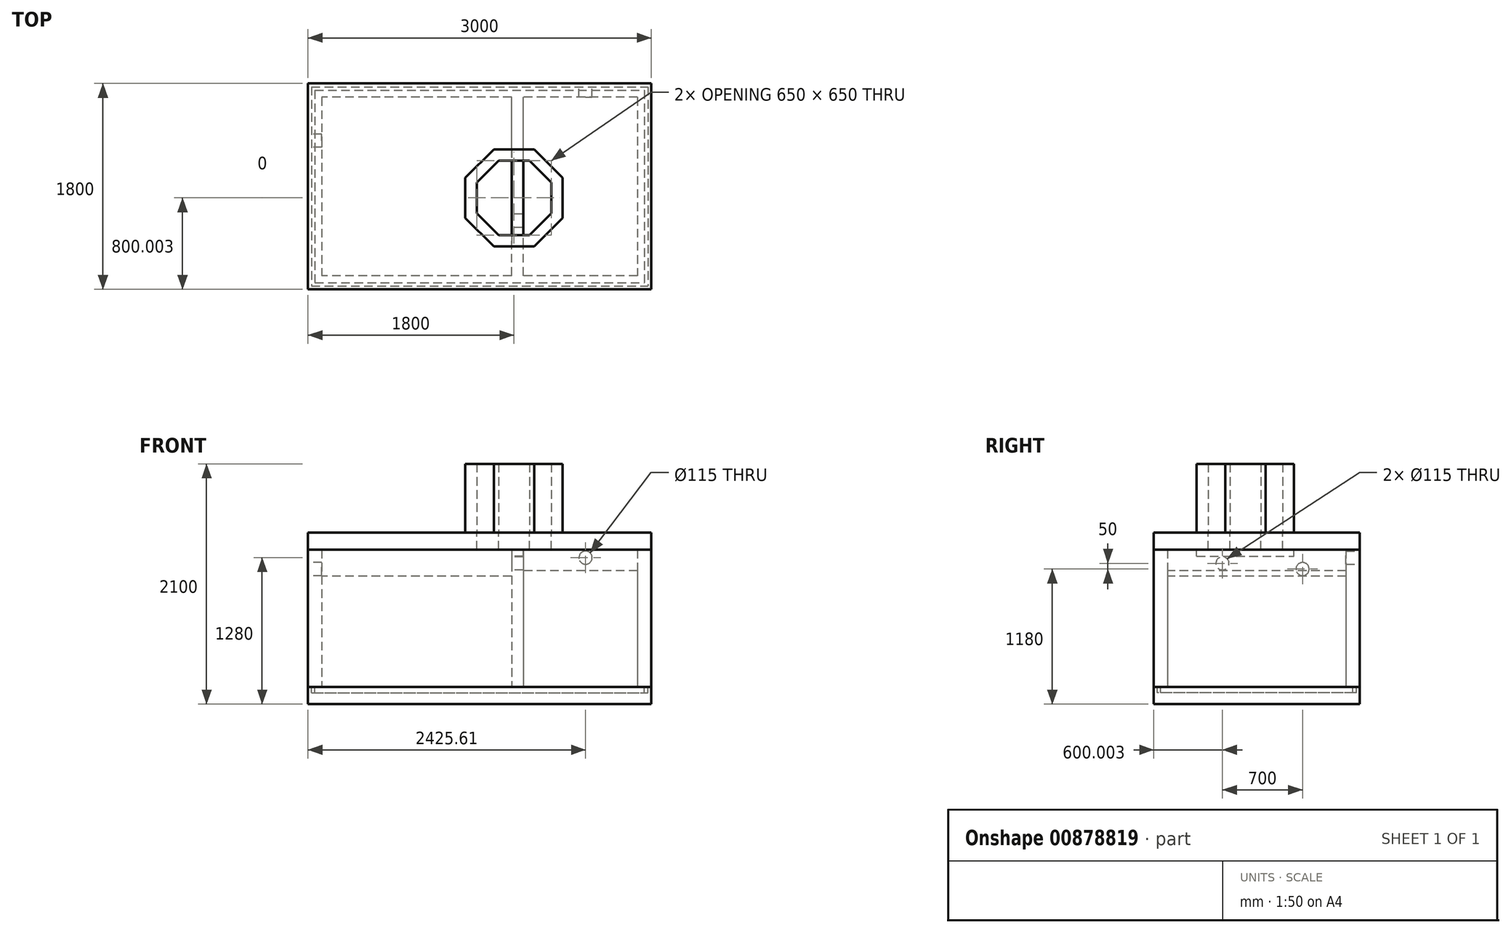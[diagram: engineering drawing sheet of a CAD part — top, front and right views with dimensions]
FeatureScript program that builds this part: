
annotation { "Feature Type Name" : "Feature", "Feature Type Description" : "" }
export const myFeature = defineFeature(function(context is Context, id is Id, definition is map)
    precondition{}
    {
        {
            var Q0;
            Q0=qCreatedBy(makeId("Top.planeOp"),FACE);
            var sketch = newSketch(context, id + "F0", { "sketchPlane" : qUnion([Q0])});
            skLineSegment(sketch, "E0.bottom", {"start": v(-1441.41, 733.1) * mm, "end": v(1558.59, 733.1) * mm});
            skLineSegment(sketch, "E0.top", {"start": v(-1441.41, -1066.9) * mm, "end": v(1558.59, -1066.9) * mm});
            skLineSegment(sketch, "E0.left", {"start": v(-1441.41, 733.1) * mm, "end": v(-1441.41, -1066.9) * mm});
            skLineSegment(sketch, "E0.right", {"start": v(1558.59, 733.1) * mm, "end": v(1558.59, -1066.9) * mm});
            skSolve(sketch);
        }
        {
            var Q0;
            Q0=makeQuery(id+"F0.imprint","IMPRINT",FACE,{"disambiguationData":[TD([[makeQuery(id+"F0.imprint","IMPRINT",EDGE,{"derivedFrom":sQuery(id+"F0.wireOp",EDGE,"E0.bottom")}),-1.0]])]});
            extrude(context, id + "F1", {"entities" : qUnion([Q0]), "depth" : 150 * mm, "offsetDistance" : 25 * mm});
        }
        {
            var Q0;
            Q0=makeQuery(id+"F1.opExtrude","CAP_FACE",FACE,{"disambiguationData":[OSD([sQuery(id+"F0.wireOp",EDGE,"E0.bottom"),sQuery(id+"F0.wireOp",EDGE,"E0.top"),sQuery(id+"F0.wireOp",EDGE,"E0.left"),sQuery(id+"F0.wireOp",EDGE,"E0.right")])],"isStart":false});
            var sketch = newSketch(context, id + "F2", { "sketchPlane" : qUnion([Q0])});
            skLineSegment(sketch, "E1.bottom", {"start": v(-1411.41, 703.1) * mm, "end": v(1528.59, 703.1) * mm});
            skLineSegment(sketch, "E1.top", {"start": v(-1411.41, -1036.9) * mm, "end": v(1528.59, -1036.9) * mm});
            skLineSegment(sketch, "E1.left", {"start": v(-1411.41, 703.1) * mm, "end": v(-1411.41, -1036.9) * mm});
            skLineSegment(sketch, "E1.right", {"start": v(1528.59, 703.1) * mm, "end": v(1528.59, -1036.9) * mm});
            skLineSegment(sketch, "E2.0", {"start": v(-1381.41, 673.1) * mm, "end": v(-1381.41, -1006.9) * mm});
            skLineSegment(sketch, "E2.1", {"start": v(-1381.41, 673.1) * mm, "end": v(1498.59, 673.1) * mm});
            skLineSegment(sketch, "E2.2", {"start": v(1498.59, 673.1) * mm, "end": v(1498.59, -1006.9) * mm});
            skLineSegment(sketch, "E2.3", {"start": v(-1381.41, -1006.9) * mm, "end": v(1498.59, -1006.9) * mm});
            skSolve(sketch);
        }
        {
            var Q0;
            Q0=makeQuery(id+"F2.imprint","IMPRINT",FACE,{"disambiguationData":[TD([[makeQuery(id+"F2.imprint","IMPRINT",EDGE,{"derivedFrom":sQuery(id+"F2.wireOp",EDGE,"E1.bottom")}),-1.0]])]});
            extrude(context, id + "F3", {"entities" : qUnion([Q0]), "operationType" : NewBodyOperationType.REMOVE, "oppositeDirection" : true, "depth" : 50 * mm, "offsetDistance" : 25 * mm});
        }
        {
            var Q0;
            {var subQ0=sQuery(id+"F0.wireOp",EDGE,"E0.left");var subQ1=sQuery(id+"F0.wireOp",EDGE,"E0.top");var subQ2=sQuery(id+"F0.wireOp",EDGE,"E0.right");var subQ3=sQuery(id+"F0.wireOp",EDGE,"E0.bottom");Q0=makeQuery(id+"F3.boolean.opBoolean","SPLIT",FACE,{"disambiguationData":[TD([makeQuery(id+"F1.opExtrude","SWEPT_FACE",FACE,{"disambiguationData":[OSD([subQ3])]})])],"derivedFrom":makeQuery(id+"F1.opExtrude","CAP_FACE",FACE,{"disambiguationData":[OSD([subQ3,subQ1,subQ0,subQ2])],"isStart":false})});}
            var sketch = newSketch(context, id + "F4", { "sketchPlane" : qUnion([Q0])});
            skLineSegment(sketch, "E3.bottom", {"start": v(1558.59, 733.1) * mm, "end": v(-1441.41, 733.1) * mm});
            skLineSegment(sketch, "E3.top", {"start": v(1558.59, -1066.9) * mm, "end": v(-1441.41, -1066.9) * mm});
            skLineSegment(sketch, "E3.left", {"start": v(1558.59, 733.1) * mm, "end": v(1558.59, -1066.9) * mm});
            skLineSegment(sketch, "E3.right", {"start": v(-1441.41, 733.1) * mm, "end": v(-1441.41, -1066.9) * mm});
            skLineSegment(sketch, "E4.0", {"start": v(1438.59, 613.1) * mm, "end": v(1438.59, -946.9) * mm});
            skLineSegment(sketch, "E4.1", {"start": v(1438.59, 613.1) * mm, "end": v(438.59, 613.1) * mm});
            skLineSegment(sketch, "E4.2", {"start": v(-1321.41, 613.1) * mm, "end": v(-1321.41, -946.9) * mm});
            skLineSegment(sketch, "E4.3", {"start": v(1438.59, -946.9) * mm, "end": v(438.59, -946.9) * mm});
            skLineSegment(sketch, "E5", {"start": v(438.59, -946.9) * mm, "end": v(438.59, 613.1) * mm});
            skLineSegment(sketch, "E6.0", {"start": v(338.59, -1166.9) * mm, "end": v(338.59, 628.91) * mm});
            skLineSegment(sketch, "E7", {"start": v(338.59, -946.9) * mm, "end": v(-1321.41, -946.9) * mm});
            skLineSegment(sketch, "E8", {"start": v(338.59, 628.91) * mm, "end": v(338.59, 633.1) * mm});
            skLineSegment(sketch, "E9", {"start": v(338.59, 628.91) * mm, "end": v(338.59, 628.91) * mm});
            skLineSegment(sketch, "E10", {"start": v(338.59, 613.1) * mm, "end": v(-1321.41, 613.1) * mm});
            skSolve(sketch);
        }
        {
            var Q0;
            Q0 = qSketchRegion(id + "F4", true);
            extrude(context, id + "F5", {"entities" : qUnion([Q0]), "depth" : 1200 * mm, "offsetDistance" : 25 * mm});
        }
        {
            var Q0;
            Q0=makeQuery(id+"F5.opExtrude","CAP_FACE",FACE,{"disambiguationData":[OSD([sQuery(id+"F4.wireOp",EDGE,"E3.bottom"),sQuery(id+"F4.wireOp",EDGE,"E3.top"),sQuery(id+"F4.wireOp",EDGE,"E3.left"),sQuery(id+"F4.wireOp",EDGE,"E3.right"),sQuery(id+"F4.wireOp",EDGE,"E4.0"),sQuery(id+"F4.wireOp",EDGE,"E4.1"),sQuery(id+"F4.wireOp",EDGE,"E4.2"),sQuery(id+"F4.wireOp",EDGE,"E4.3"),sQuery(id+"F4.wireOp",EDGE,"E5"),sQuery(id+"F4.wireOp",EDGE,"E6.0"),sQuery(id+"F4.wireOp",EDGE,"E7"),sQuery(id+"F4.wireOp",EDGE,"E8"),sQuery(id+"F4.wireOp",EDGE,"E10")])],"isStart":false});
            var sketch = newSketch(context, id + "F6", { "sketchPlane" : qUnion([Q0])});
            skLineSegment(sketch, "E11.bottom", {"start": v(-1441.41, 733.1) * mm, "end": v(1558.59, 733.1) * mm});
            skLineSegment(sketch, "E11.top", {"start": v(-1441.41, -1066.9) * mm, "end": v(1558.59, -1066.9) * mm});
            skLineSegment(sketch, "E11.left", {"start": v(-1441.41, 733.1) * mm, "end": v(-1441.41, -1066.9) * mm});
            skLineSegment(sketch, "E11.right", {"start": v(1558.59, 733.1) * mm, "end": v(1558.59, -1066.9) * mm});
            skSolve(sketch);
        }
        {
            var Q0;
            Q0 = qSketchRegion(id + "F6", true);
            extrude(context, id + "F7", {"entities" : qUnion([Q0]), "depth" : 150 * mm, "offsetDistance" : 25 * mm});
        }
        {
            var Q0;
            Q0=makeQuery(id+"F5.opExtrude","SWEPT_FACE",FACE,{"disambiguationData":[OSD([sQuery(id+"F4.wireOp",EDGE,"E3.bottom")])]});
            var sketch = newSketch(context, id + "F8", { "sketchPlane" : qUnion([Q0])});
            skPoint(sketch, "E12", {"position": v(-984.2, 1280) * mm});
            skCircle(sketch, "E13", {"center": v(-984.2, 1280) * mm, "radius": 57.5 * mm});
            skSolve(sketch);
        }
        {
            var Q0;
            Q0=makeQuery(id+"F8.imprint","IMPRINT",FACE,{"disambiguationData":[TD([[makeQuery(id+"F8.imprint","IMPRINT",EDGE,{"derivedFrom":sQuery(id+"F8.wireOp",EDGE,"E13")}),1.0]])]});
            extrude(context, id + "F9", {"entities" : qUnion([Q0]), "operationType" : NewBodyOperationType.REMOVE, "oppositeDirection" : true, "depth" : 390 * mm, "offsetDistance" : 25 * mm});
        }
        {
            var Q0;
            Q0=makeQuery(id+"F5.opExtrude","SWEPT_FACE",FACE,{"disambiguationData":[OSD([sQuery(id+"F4.wireOp",EDGE,"E6.0"),sQuery(id+"F4.wireOp",EDGE,"E8")])]});
            var sketch = newSketch(context, id + "F10", { "sketchPlane" : qUnion([Q0])});
            skPoint(sketch, "E14", {"position": v(466.9, 1230) * mm});
            skCircle(sketch, "E15", {"center": v(466.9, 1230) * mm, "radius": 57.5 * mm});
            skSolve(sketch);
        }
        {
            var Q0;
            Q0=makeQuery(id+"F10.imprint","IMPRINT",FACE,{"disambiguationData":[TD([[makeQuery(id+"F10.imprint","IMPRINT",EDGE,{"derivedFrom":sQuery(id+"F10.wireOp",EDGE,"E15")}),1.0]])]});
            extrude(context, id + "F11", {"entities" : qUnion([Q0]), "operationType" : NewBodyOperationType.REMOVE, "oppositeDirection" : true, "depth" : 430 * mm, "offsetDistance" : 25 * mm});
        }
        {
            var Q0;
            Q0=makeQuery(id+"F5.opExtrude","SWEPT_FACE",FACE,{"disambiguationData":[OSD([sQuery(id+"F4.wireOp",EDGE,"E3.right")])]});
            var sketch = newSketch(context, id + "F12", { "sketchPlane" : qUnion([Q0])});
            skPoint(sketch, "E16", {"position": v(-233.1, 1180) * mm});
            skCircle(sketch, "E17", {"center": v(-233.1, 1180) * mm, "radius": 57.5 * mm});
            skSolve(sketch);
        }
        {
            var Q0;
            Q0=makeQuery(id+"F12.imprint","IMPRINT",FACE,{"disambiguationData":[TD([[makeQuery(id+"F12.imprint","IMPRINT",EDGE,{"derivedFrom":sQuery(id+"F12.wireOp",EDGE,"E17")}),1.0]])]});
            extrude(context, id + "F13", {"entities" : qUnion([Q0]), "operationType" : NewBodyOperationType.REMOVE, "oppositeDirection" : true, "depth" : 660 * mm, "offsetDistance" : 25 * mm});
        }
        {
            var Q0;
            Q0=makeQuery(id+"F7.opExtrude","CAP_FACE",FACE,{"disambiguationData":[OSD([sQuery(id+"F6.wireOp",EDGE,"E11.bottom"),sQuery(id+"F6.wireOp",EDGE,"E11.top"),sQuery(id+"F6.wireOp",EDGE,"E11.left"),sQuery(id+"F6.wireOp",EDGE,"E11.right")])],"isStart":false});
            var sketch = newSketch(context, id + "F14", { "sketchPlane" : qUnion([Q0])});
            skCircle(sketch, "E18.cCircle", {"center": v(358.59, -266.9) * mm, "radius": 425 * mm, "construction": true});
            skLineSegment(sketch, "E18.0", {"start": v(-66.41, -90.87) * mm, "end": v(182.55, 158.1) * mm});
            skLineSegment(sketch, "E18.1", {"start": v(182.55, 158.1) * mm, "end": v(534.63, 158.1) * mm});
            skLineSegment(sketch, "E18.2", {"start": v(534.63, 158.1) * mm, "end": v(783.59, -90.87) * mm});
            skLineSegment(sketch, "E18.3", {"start": v(783.59, -90.87) * mm, "end": v(783.59, -442.95) * mm});
            skLineSegment(sketch, "E18.4", {"start": v(783.59, -442.95) * mm, "end": v(534.63, -691.9) * mm});
            skLineSegment(sketch, "E18.5", {"start": v(534.63, -691.9) * mm, "end": v(182.55, -691.9) * mm});
            skLineSegment(sketch, "E18.6", {"start": v(182.55, -691.9) * mm, "end": v(-66.41, -442.95) * mm});
            skLineSegment(sketch, "E18.7", {"start": v(-66.41, -442.95) * mm, "end": v(-66.41, -90.87) * mm});
            skPoint(sketch, "E18.0.midPoint", {"position": v(58.07, 33.61) * mm});
            skLineSegment(sketch, "E19.0", {"start": v(33.59, -401.53) * mm, "end": v(33.59, -132.29) * mm});
            skLineSegment(sketch, "E19.1", {"start": v(223.97, -591.9) * mm, "end": v(33.59, -401.53) * mm});
            skLineSegment(sketch, "E19.2", {"start": v(33.59, -132.29) * mm, "end": v(223.97, 58.1) * mm});
            skLineSegment(sketch, "E19.3", {"start": v(493.2, -591.9) * mm, "end": v(223.97, -591.9) * mm});
            skLineSegment(sketch, "E19.4", {"start": v(223.97, 58.1) * mm, "end": v(493.2, 58.1) * mm});
            skLineSegment(sketch, "E19.5", {"start": v(493.2, 58.1) * mm, "end": v(683.59, -132.29) * mm});
            skLineSegment(sketch, "E19.6", {"start": v(683.59, -132.29) * mm, "end": v(683.59, -401.53) * mm});
            skLineSegment(sketch, "E19.7", {"start": v(683.59, -401.53) * mm, "end": v(493.2, -591.9) * mm});
            skLineSegment(sketch, "E20.0.0", {"start": v(1558.59, 733.1) * mm, "end": v(-1441.41, 733.1) * mm});
            skLineSegment(sketch, "E20.0.1", {"start": v(-1441.41, 733.1) * mm, "end": v(-1441.41, -1066.9) * mm});
            skLineSegment(sketch, "E20.0.2", {"start": v(-1441.41, -1066.9) * mm, "end": v(1558.59, -1066.9) * mm});
            skLineSegment(sketch, "E20.0.3", {"start": v(1558.59, -1066.9) * mm, "end": v(1558.59, 733.1) * mm});
            skSolve(sketch);
        }
        {
            var Q0;
            Q0=makeQuery(id+"F14.imprint","IMPRINT",FACE,{"disambiguationData":[TD([[makeQuery(id+"F14.imprint","IMPRINT",EDGE,{"derivedFrom":sQuery(id+"F14.wireOp",EDGE,"E19.0")}),-1.0]])]});
            extrude(context, id + "F15", {"entities" : qUnion([Q0]), "operationType" : NewBodyOperationType.REMOVE, "endBound" : BoundingType.UP_TO_NEXT, "oppositeDirection" : true, "depth" : 25 * mm, "offsetDistance" : 25 * mm});
        }
        {
            var Q0;
            Q0=makeQuery(id+"F14.imprint","IMPRINT",FACE,{"disambiguationData":[TD([[makeQuery(id+"F14.imprint","IMPRINT",EDGE,{"derivedFrom":sQuery(id+"F14.wireOp",EDGE,"E18.0")}),-1.0]])]});
            extrude(context, id + "F16", {"entities" : qUnion([Q0]), "depth" : 600 * mm, "offsetDistance" : 25 * mm});
        }
        {
            var Q0;
            Q0=makeQuery(id+"F5.opExtrude","SWEPT_FACE",FACE,{"disambiguationData":[OSD([sQuery(id+"F4.wireOp",EDGE,"E6.0")])]});
            var sketch = newSketch(context, id + "F17", { "sketchPlane" : qUnion([Q0])});
            skLineSegment(sketch, "E21.0", {"start": v(-158.1, 2100) * mm, "end": v(-158.1, 1500) * mm});
            skLineSegment(sketch, "E22.0", {"start": v(691.9, 2100) * mm, "end": v(691.9, 1500) * mm});
            skLineSegment(sketch, "E23.bottom", {"start": v(-158.1, 1500) * mm, "end": v(691.9, 1500) * mm});
            skLineSegment(sketch, "E23.top", {"start": v(-158.1, 1500) * mm, "end": v(691.9, 1500) * mm});
            skLineSegment(sketch, "E23.left", {"start": v(-158.1, 1500) * mm, "end": v(-158.1, 1500) * mm});
            skLineSegment(sketch, "E23.right", {"start": v(691.9, 1500) * mm, "end": v(691.9, 1500) * mm});
            skLineSegment(sketch, "E24", {"start": v(-158.1, 1500) * mm, "end": v(-158.1, 1237.18) * mm, "construction": true});
            skLineSegment(sketch, "E25", {"start": v(691.9, 1500) * mm, "end": v(691.9, 1209.25) * mm, "construction": true});
            skLineSegment(sketch, "E26.bottom", {"start": v(-158.1, 1350) * mm, "end": v(691.9, 1350) * mm});
            skLineSegment(sketch, "E26.top", {"start": v(-158.1, 1293.04) * mm, "end": v(691.9, 1293.04) * mm});
            skLineSegment(sketch, "E26.left", {"start": v(-158.1, 1350) * mm, "end": v(-158.1, 1293.04) * mm});
            skLineSegment(sketch, "E26.right", {"start": v(691.9, 1350) * mm, "end": v(691.9, 1293.04) * mm});
            skSolve(sketch);
        }
        {
            var Q0;
            Q0=makeQuery(id+"F17.imprint","IMPRINT",FACE,{"disambiguationData":[TD([[makeQuery(id+"F17.imprint","IMPRINT",EDGE,{"derivedFrom":sQuery(id+"F17.wireOp",EDGE,"E26.bottom")}),1.0]])]});
            extrude(context, id + "F18", {"entities" : qUnion([Q0]), "operationType" : NewBodyOperationType.REMOVE, "endBound" : BoundingType.UP_TO_NEXT, "oppositeDirection" : true, "depth" : 25 * mm, "offsetDistance" : 25 * mm});
        }
        {
            var Q0;
            Q0=makeQuery(id+"F3.boolean.opBoolean","SPLIT",FACE,{"disambiguationData":[TD([makeQuery(id+"F3.opExtrude","SWEPT_FACE",FACE,{"disambiguationData":[OSD([sQuery(id+"F2.wireOp",EDGE,"E2.0")])]})])],"derivedFrom":makeQuery(id+"F1.opExtrude","CAP_FACE",FACE,{"disambiguationData":[OSD([sQuery(id+"F0.wireOp",EDGE,"E0.bottom"),sQuery(id+"F0.wireOp",EDGE,"E0.top"),sQuery(id+"F0.wireOp",EDGE,"E0.left"),sQuery(id+"F0.wireOp",EDGE,"E0.right")])],"isStart":false})});
            var sketch = newSketch(context, id + "F19", { "sketchPlane" : qUnion([Q0])});
            skLineSegment(sketch, "E27.0", {"start": v(-1321.41, 613.1) * mm, "end": v(-1321.41, -946.9) * mm});
            skLineSegment(sketch, "E28.0", {"start": v(338.59, 613.1) * mm, "end": v(-1321.41, 613.1) * mm});
            skLineSegment(sketch, "E29.0", {"start": v(338.59, -946.9) * mm, "end": v(-1321.41, -946.9) * mm});
            skLineSegment(sketch, "E30.0", {"start": v(338.59, -946.9) * mm, "end": v(338.59, 613.1) * mm});
            skSolve(sketch);
        }
        {
            var Q0;
            Q0=makeQuery(id+"F19.imprint","IMPRINT",FACE,{"disambiguationData":[TD([[makeQuery(id+"F19.imprint","IMPRINT",EDGE,{"derivedFrom":sQuery(id+"F19.wireOp",EDGE,"E27.0")}),-1.0]])]});
            var sketch = newSketch(context, id + "F20", { "sketchPlane" : qUnion([Q0])});
            skLineSegment(sketch, "E31.0", {"start": v(1438.59, 613.1) * mm, "end": v(438.59, 613.1) * mm});
            skLineSegment(sketch, "E32.0", {"start": v(1438.59, 613.1) * mm, "end": v(1438.59, -946.9) * mm});
            skLineSegment(sketch, "E33.0", {"start": v(1438.59, -946.9) * mm, "end": v(438.59, -946.9) * mm});
            skLineSegment(sketch, "E34.0", {"start": v(438.59, -946.9) * mm, "end": v(438.59, 613.1) * mm});
            skSolve(sketch);
        }
        {
            var Q0;
            Q0=makeQuery(id+"F20.imprint","IMPRINT",FACE,{"disambiguationData":[TD([[makeQuery(id+"F20.imprint","IMPRINT",EDGE,{"derivedFrom":sQuery(id+"F20.wireOp",EDGE,"E31.0")}),1.0]])]});
            var Q1;
            Q1=makeQuery(id+"F5.opExtrude","CAP_FACE",FACE,{"disambiguationData":[OSD([sQuery(id+"F4.wireOp",EDGE,"E3.bottom"),sQuery(id+"F4.wireOp",EDGE,"E3.top"),sQuery(id+"F4.wireOp",EDGE,"E3.left"),sQuery(id+"F4.wireOp",EDGE,"E3.right"),sQuery(id+"F4.wireOp",EDGE,"E4.0"),sQuery(id+"F4.wireOp",EDGE,"E4.1"),sQuery(id+"F4.wireOp",EDGE,"E4.2"),sQuery(id+"F4.wireOp",EDGE,"E4.3"),sQuery(id+"F4.wireOp",EDGE,"E5"),sQuery(id+"F4.wireOp",EDGE,"E6.0"),sQuery(id+"F4.wireOp",EDGE,"E7"),sQuery(id+"F4.wireOp",EDGE,"E10")])],"isStart":false});
            extrude(context, id + "F21", {"entities" : qUnion([Q0]), "depth" : 1015 * mm, "endBoundEntityFace" : qUnion([Q1]), "offsetDistance" : 25 * mm});
        }
        {
            var Q0;
            Q0=makeQuery(id+"F19.imprint","IMPRINT",FACE,{"disambiguationData":[TD([[makeQuery(id+"F19.imprint","IMPRINT",EDGE,{"derivedFrom":sQuery(id+"F19.wireOp",EDGE,"E27.0")}),1.0]])]});
            var Q1;
            Q1=makeQuery(id+"F5.opExtrude","CAP_FACE",FACE,{"disambiguationData":[OSD([sQuery(id+"F4.wireOp",EDGE,"E3.bottom"),sQuery(id+"F4.wireOp",EDGE,"E3.top"),sQuery(id+"F4.wireOp",EDGE,"E3.left"),sQuery(id+"F4.wireOp",EDGE,"E3.right"),sQuery(id+"F4.wireOp",EDGE,"E4.0"),sQuery(id+"F4.wireOp",EDGE,"E4.1"),sQuery(id+"F4.wireOp",EDGE,"E4.2"),sQuery(id+"F4.wireOp",EDGE,"E4.3"),sQuery(id+"F4.wireOp",EDGE,"E5"),sQuery(id+"F4.wireOp",EDGE,"E6.0"),sQuery(id+"F4.wireOp",EDGE,"E7"),sQuery(id+"F4.wireOp",EDGE,"E10")])],"isStart":false});
            extrude(context, id + "F22", {"entities" : qUnion([Q0]), "depth" : 969 * mm, "endBoundEntityFace" : qUnion([Q1]), "offsetDistance" : 25 * mm});
        }
        {
            var Q0;
            Q0=makeQuery(id+"F1.opExtrude","SWEPT_FACE",FACE,{"disambiguationData":[OSD([sQuery(id+"F0.wireOp",EDGE,"E0.top")])]});
            var sketch = newSketch(context, id + "F23", { "sketchPlane" : qUnion([Q0])});
            skLineSegment(sketch, "E35", {"start": v(-1391.41, 40) * mm, "end": v(458.59, 40) * mm});
            skLineSegment(sketch, "E36", {"start": v(-1401.41, 50) * mm, "end": v(-1401.41, 1140) * mm});
            skPoint(sketch, "E37.visualSharp", {"position": v(-1401.41, 40) * mm});
            skArc(sketch, "E37.filletArc", {"start": v(-1401.41, 50) * mm, "mid": v(-1398.48, 42.93) * mm, "end": v(-1391.41, 40) * mm});
            skSolve(sketch);
        }
        {
            var Q0;
            Q0=makeQuery(id+"F1.opExtrude","SWEPT_FACE",FACE,{"disambiguationData":[OSD([sQuery(id+"F0.wireOp",EDGE,"E0.right")])]});
            var Q1;
            Q1=sQuery(id+"F23.wireOp",VERTEX,"E35.end");
            cPlane(context, id + "F24", {"entities" : qUnion([Q0, Q1]), "cplaneType" : CPlaneType.PLANE_POINT, "offset" : 25 * mm, "width" : 150 * mm, "height" : 150 * mm});
        }
        {
            var Q0;
            Q0=makeQuery(id+"F3.boolean.opBoolean","SPLIT",FACE,{"disambiguationData":[TD([makeQuery(id+"F3.opExtrude","SWEPT_FACE",FACE,{"disambiguationData":[OSD([sQuery(id+"F2.wireOp",EDGE,"E2.0")])]})])],"derivedFrom":makeQuery(id+"F1.opExtrude","CAP_FACE",FACE,{"disambiguationData":[OSD([sQuery(id+"F0.wireOp",EDGE,"E0.bottom"),sQuery(id+"F0.wireOp",EDGE,"E0.top"),sQuery(id+"F0.wireOp",EDGE,"E0.left"),sQuery(id+"F0.wireOp",EDGE,"E0.right")])],"isStart":false})});
            var sketch = newSketch(context, id + "F25", { "sketchPlane" : qUnion([Q0])});
            skLineSegment(sketch, "E38", {"start": v(-1328.84, 607.24) * mm, "end": v(1426.47, 607.24) * mm});
            skLineSegment(sketch, "E39.0.1.0", {"start": v(-1328.84, 357.24) * mm, "end": v(1426.47, 357.24) * mm});
            skLineSegment(sketch, "E39.0.2.0", {"start": v(-1328.84, 107.24) * mm, "end": v(1426.47, 107.24) * mm});
            skLineSegment(sketch, "E39.0.3.0", {"start": v(-1328.84, -142.76) * mm, "end": v(1426.47, -142.76) * mm});
            skLineSegment(sketch, "E39.0.4.0", {"start": v(-1328.84, -392.76) * mm, "end": v(1426.47, -392.76) * mm});
            skLineSegment(sketch, "E39.0.5.0", {"start": v(-1328.84, -642.76) * mm, "end": v(1426.47, -642.76) * mm});
            skLineSegment(sketch, "E39.0.6.0", {"start": v(-1328.84, -892.76) * mm, "end": v(1426.47, -892.76) * mm});
            skLineSegment(sketch, "E39.direction1", {"start": v(-1328.84, 607.24) * mm, "end": v(-1303.84, 607.24) * mm, "construction": true});
            skLineSegment(sketch, "E39.direction2", {"start": v(-1328.84, 607.24) * mm, "end": v(-1328.84, 357.24) * mm, "construction": true});
            skLineSegment(sketch, "E40", {"start": v(-1279.85, 673.1) * mm, "end": v(-1279.85, -961.56) * mm});
            skLineSegment(sketch, "E41.1.0.0", {"start": v(-1029.85, 673.1) * mm, "end": v(-1029.85, -961.56) * mm});
            skLineSegment(sketch, "E41.2.0.0", {"start": v(-779.85, 673.1) * mm, "end": v(-779.85, -961.56) * mm});
            skLineSegment(sketch, "E41.3.0.0", {"start": v(-529.85, 673.1) * mm, "end": v(-529.85, -961.56) * mm});
            skLineSegment(sketch, "E41.4.0.0", {"start": v(-279.85, 673.1) * mm, "end": v(-279.85, -961.56) * mm});
            skLineSegment(sketch, "E41.5.0.0", {"start": v(-29.85, 673.1) * mm, "end": v(-29.85, -961.56) * mm});
            skLineSegment(sketch, "E41.6.0.0", {"start": v(220.15, 673.1) * mm, "end": v(220.15, -961.56) * mm});
            skLineSegment(sketch, "E41.7.0.0", {"start": v(470.15, 673.1) * mm, "end": v(470.15, -961.56) * mm});
            skLineSegment(sketch, "E41.8.0.0", {"start": v(720.15, 673.1) * mm, "end": v(720.15, -961.56) * mm});
            skLineSegment(sketch, "E41.9.0.0", {"start": v(970.15, 673.1) * mm, "end": v(970.15, -961.56) * mm});
            skLineSegment(sketch, "E41.10.0.0", {"start": v(1220.15, 673.1) * mm, "end": v(1220.15, -961.56) * mm});
            skLineSegment(sketch, "E41.11.0.0", {"start": v(1470.15, 673.1) * mm, "end": v(1470.15, -961.56) * mm});
            skLineSegment(sketch, "E41.direction1", {"start": v(-1279.85, -961.56) * mm, "end": v(-1029.85, -961.56) * mm, "construction": true});
            skSolve(sketch);
        }
    });
